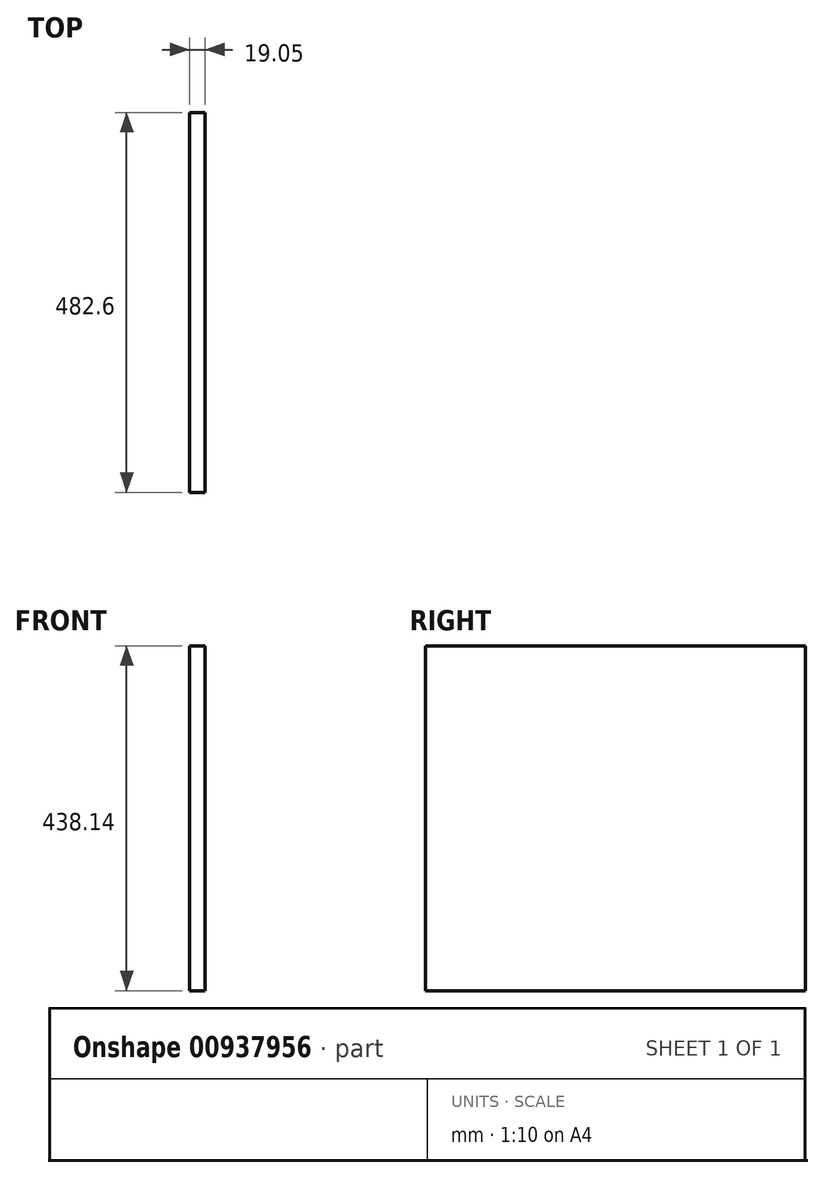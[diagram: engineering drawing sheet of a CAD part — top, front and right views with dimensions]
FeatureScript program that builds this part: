
annotation { "Feature Type Name" : "Feature", "Feature Type Description" : "" }
export const myFeature = defineFeature(function(context is Context, id is Id, definition is map)
    precondition{}
    {
        {
            var Q0;
            Q0=qCreatedBy(makeId("Right.planeOp"),FACE);
            var sketch = newSketch(context, id + "F0", { "sketchPlane" : qUnion([Q0])});
            skLineSegment(sketch, "E0.bottom", {"start": v(241.3, 219.08) * mm, "end": v(-241.3, 219.08) * mm});
            skLineSegment(sketch, "E0.top", {"start": v(241.3, -219.08) * mm, "end": v(-241.3, -219.08) * mm});
            skLineSegment(sketch, "E0.left", {"start": v(241.3, 219.07) * mm, "end": v(241.3, -219.08) * mm});
            skLineSegment(sketch, "E0.right", {"start": v(-241.3, 219.08) * mm, "end": v(-241.3, -219.08) * mm});
            skPoint(sketch, "E0.middle", {"position": v(0, 0) * mm});
            skSolve(sketch);
        }
        {
            var Q0;
            Q0=makeQuery(id+"F0.imprint","IMPRINT",FACE,{"disambiguationData":[TD([[makeQuery(id+"F0.imprint","IMPRINT",EDGE,{"derivedFrom":sQuery(id+"F0.wireOp",EDGE,"E0.bottom")}),1.0]])]});
            extrude(context, id + "F1", {"entities" : qUnion([Q0]), "depth" : 19.05 * mm, "offsetDistance" : 25.4 * mm});
        }
    });
